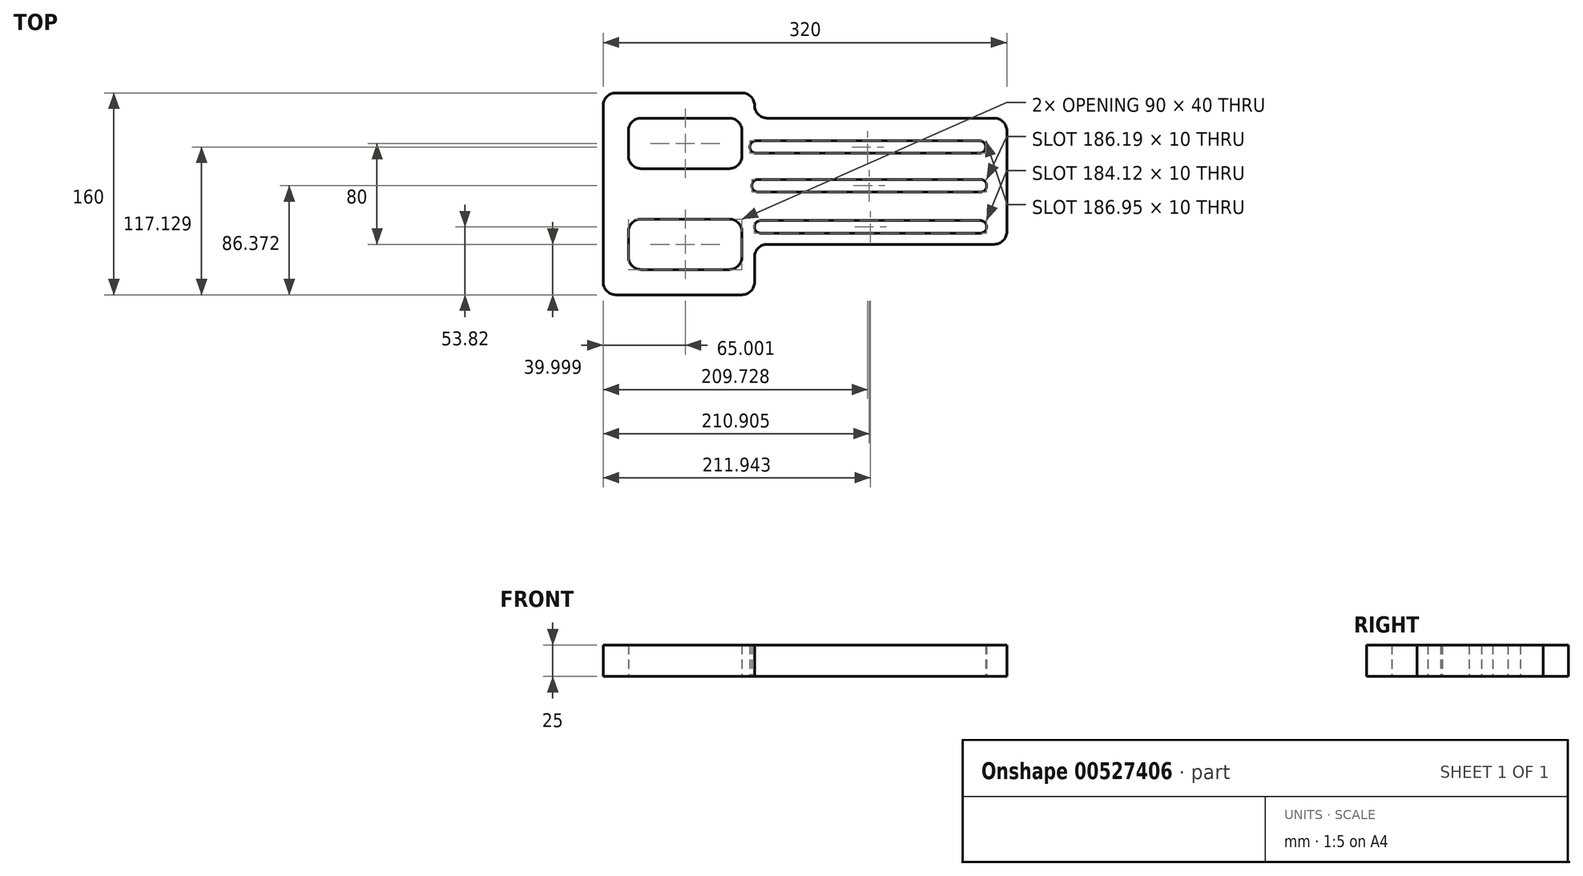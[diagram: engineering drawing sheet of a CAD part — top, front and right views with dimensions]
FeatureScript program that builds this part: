
annotation { "Feature Type Name" : "Feature", "Feature Type Description" : "" }
export const myFeature = defineFeature(function(context is Context, id is Id, definition is map)
    precondition{}
    {
        {
            var Q0;
            Q0=qCreatedBy(makeId("Top.planeOp"),FACE);
            var sketch = newSketch(context, id + "F0", { "sketchPlane" : qUnion([Q0])});
            skLineSegment(sketch, "E0", {"start": v(-39.68, 42.28) * mm, "end": v(-39.68, -97.72) * mm});
            skLineSegment(sketch, "E1", {"start": v(-29.68, 52.28) * mm, "end": v(70.32, 52.28) * mm});
            skLineSegment(sketch, "E2", {"start": v(-29.68, -107.72) * mm, "end": v(70.32, -107.72) * mm});
            skLineSegment(sketch, "E3.bottom", {"start": v(-9.68, 32.28) * mm, "end": v(60.32, 32.28) * mm});
            skLineSegment(sketch, "E3.top", {"start": v(-9.68, -7.72) * mm, "end": v(60.32, -7.72) * mm});
            skLineSegment(sketch, "E3.left", {"start": v(-19.68, 22.28) * mm, "end": v(-19.68, 2.28) * mm});
            skLineSegment(sketch, "E3.right", {"start": v(70.32, 22.28) * mm, "end": v(70.32, 2.28) * mm});
            skLineSegment(sketch, "E4.bottom", {"start": v(-9.68, -47.72) * mm, "end": v(60.32, -47.72) * mm});
            skLineSegment(sketch, "E4.top", {"start": v(-9.68, -87.72) * mm, "end": v(60.32, -87.72) * mm});
            skLineSegment(sketch, "E4.left", {"start": v(-19.68, -57.72) * mm, "end": v(-19.68, -77.72) * mm});
            skLineSegment(sketch, "E4.right", {"start": v(70.32, -57.72) * mm, "end": v(70.32, -77.72) * mm});
            skLineSegment(sketch, "E5", {"start": v(80.32, 42.28) * mm, "end": v(80.32, 42.28) * mm});
            skLineSegment(sketch, "E6", {"start": v(80.32, -97.72) * mm, "end": v(80.32, -77.72) * mm});
            skLineSegment(sketch, "E7", {"start": v(90.32, -67.72) * mm, "end": v(270.32, -67.72) * mm});
            skLineSegment(sketch, "E8", {"start": v(90.32, 32.28) * mm, "end": v(270.32, 32.28) * mm});
            skLineSegment(sketch, "E9", {"start": v(280.32, 22.28) * mm, "end": v(280.32, -57.72) * mm});
            skLineSegment(sketch, "E10", {"start": v(81.57, 4.4) * mm, "end": v(258.52, 4.4) * mm});
            skLineSegment(sketch, "E11", {"start": v(258.52, 14.4) * mm, "end": v(81.57, 14.4) * mm});
            skLineSegment(sketch, "E12", {"start": v(83.13, -26.35) * mm, "end": v(259.32, -26.35) * mm});
            skLineSegment(sketch, "E13", {"start": v(259.32, -16.35) * mm, "end": v(83.13, -16.35) * mm});
            skLineSegment(sketch, "E14", {"start": v(85.2, -58.9) * mm, "end": v(259.32, -58.9) * mm});
            skLineSegment(sketch, "E15", {"start": v(259.32, -48.9) * mm, "end": v(85.2, -48.9) * mm});
            skPoint(sketch, "E16.visualSharp", {"position": v(-39.68, 52.28) * mm});
            skArc(sketch, "E16.filletArc", {"start": v(-29.68, 52.28) * mm, "mid": v(-36.75, 49.35) * mm, "end": v(-39.68, 42.28) * mm});
            skPoint(sketch, "E17.visualSharp", {"position": v(-39.68, -107.72) * mm});
            skArc(sketch, "E17.filletArc", {"start": v(-39.68, -97.72) * mm, "mid": v(-36.75, -104.8) * mm, "end": v(-29.68, -107.72) * mm});
            skPoint(sketch, "E18.visualSharp", {"position": v(80.32, -107.72) * mm});
            skArc(sketch, "E18.filletArc", {"start": v(70.32, -107.72) * mm, "mid": v(77.4, -104.8) * mm, "end": v(80.32, -97.72) * mm});
            skPoint(sketch, "E19.visualSharp", {"position": v(80.32, -67.72) * mm});
            skArc(sketch, "E19.filletArc", {"start": v(90.32, -67.72) * mm, "mid": v(83.25, -70.65) * mm, "end": v(80.32, -77.72) * mm});
            skPoint(sketch, "E20.visualSharp", {"position": v(280.32, -67.72) * mm});
            skArc(sketch, "E20.filletArc", {"start": v(270.32, -67.72) * mm, "mid": v(277.4, -64.8) * mm, "end": v(280.32, -57.72) * mm});
            skArc(sketch, "E21", {"start": v(81.57, 14.4) * mm, "mid": v(76.57, 9.4) * mm, "end": v(81.57, 4.4) * mm});
            skArc(sketch, "E22", {"start": v(83.13, -16.35) * mm, "mid": v(78.13, -21.35) * mm, "end": v(83.13, -26.35) * mm});
            skArc(sketch, "E23", {"start": v(259.32, -16.35) * mm, "mid": v(264.32, -21.35) * mm, "end": v(259.32, -26.35) * mm});
            skArc(sketch, "E24", {"start": v(259.32, -48.9) * mm, "mid": v(264.32, -53.9) * mm, "end": v(259.32, -58.9) * mm});
            skArc(sketch, "E25", {"start": v(85.2, -48.9) * mm, "mid": v(80.2, -53.9) * mm, "end": v(85.2, -58.9) * mm});
            skPoint(sketch, "E26.visualSharp", {"position": v(80.32, 52.28) * mm});
            skArc(sketch, "E26.filletArc", {"start": v(80.32, 42.28) * mm, "mid": v(77.4, 49.35) * mm, "end": v(70.32, 52.28) * mm});
            skPoint(sketch, "E27.visualSharp", {"position": v(80.32, 32.28) * mm});
            skArc(sketch, "E27.filletArc", {"start": v(80.32, 42.28) * mm, "mid": v(83.25, 35.2) * mm, "end": v(90.32, 32.28) * mm});
            skPoint(sketch, "E28.visualSharp", {"position": v(280.32, 32.28) * mm});
            skArc(sketch, "E28.filletArc", {"start": v(280.32, 22.28) * mm, "mid": v(277.4, 29.35) * mm, "end": v(270.32, 32.28) * mm});
            skPoint(sketch, "E29.visualSharp", {"position": v(-19.68, -7.72) * mm});
            skArc(sketch, "E29.filletArc", {"start": v(-19.68, 2.28) * mm, "mid": v(-16.75, -4.8) * mm, "end": v(-9.68, -7.72) * mm});
            skPoint(sketch, "E30.visualSharp", {"position": v(-19.68, 32.28) * mm});
            skArc(sketch, "E30.filletArc", {"start": v(-9.68, 32.28) * mm, "mid": v(-16.75, 29.35) * mm, "end": v(-19.68, 22.28) * mm});
            skPoint(sketch, "E31.visualSharp", {"position": v(70.32, 32.28) * mm});
            skArc(sketch, "E31.filletArc", {"start": v(70.32, 22.28) * mm, "mid": v(67.4, 29.35) * mm, "end": v(60.32, 32.28) * mm});
            skPoint(sketch, "E32.visualSharp", {"position": v(70.32, -7.72) * mm});
            skArc(sketch, "E32.filletArc", {"start": v(60.32, -7.72) * mm, "mid": v(67.4, -4.8) * mm, "end": v(70.32, 2.28) * mm});
            skPoint(sketch, "E33.visualSharp", {"position": v(70.32, -47.72) * mm});
            skArc(sketch, "E33.filletArc", {"start": v(70.32, -57.72) * mm, "mid": v(67.4, -50.65) * mm, "end": v(60.32, -47.72) * mm});
            skPoint(sketch, "E34.visualSharp", {"position": v(70.32, -87.72) * mm});
            skArc(sketch, "E34.filletArc", {"start": v(60.32, -87.72) * mm, "mid": v(67.4, -84.8) * mm, "end": v(70.32, -77.72) * mm});
            skPoint(sketch, "E35.visualSharp", {"position": v(-19.68, -47.72) * mm});
            skArc(sketch, "E35.filletArc", {"start": v(-9.68, -47.72) * mm, "mid": v(-16.75, -50.65) * mm, "end": v(-19.68, -57.72) * mm});
            skPoint(sketch, "E36.visualSharp", {"position": v(-19.68, -87.72) * mm});
            skArc(sketch, "E36.filletArc", {"start": v(-19.68, -77.72) * mm, "mid": v(-16.75, -84.8) * mm, "end": v(-9.68, -87.72) * mm});
            skArc(sketch, "E37", {"start": v(258.52, 14.4) * mm, "mid": v(263.52, 9.4) * mm, "end": v(258.52, 4.4) * mm});
            skSolve(sketch);
        }
        {
            var Q0;
            Q0 = qSketchRegion(id + "F0", true);
            extrude(context, id + "F1", {"entities" : qUnion([Q0]), "depth" : 25 * mm, "offsetDistance" : 25 * mm});
        }
    });
